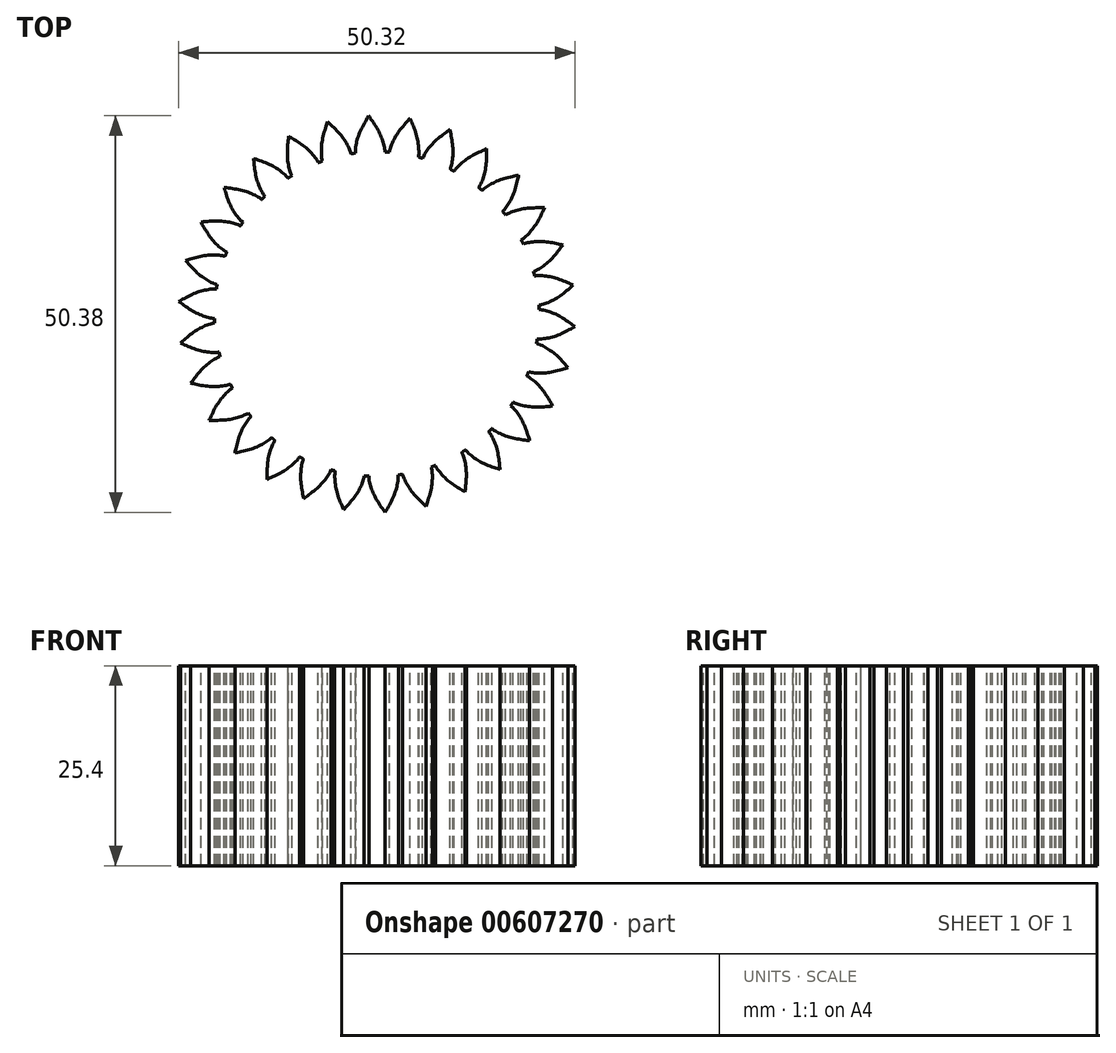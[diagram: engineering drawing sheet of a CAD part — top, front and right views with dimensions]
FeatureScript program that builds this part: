
annotation { "Feature Type Name" : "Feature", "Feature Type Description" : "" }
export const myFeature = defineFeature(function(context is Context, id is Id, definition is map)
    precondition{}
    {
        {
            assignVariable(context, id + "F0", {"name" : "nt", "anyValue" : 30});
        }
        {
            var Q0;
            Q0=qCreatedBy(makeId("Top.planeOp"),FACE);
            var sketch = newSketch(context, id + "F1", { "sketchPlane" : qUnion([Q0])});
            skPoint(sketch, "E0", {"position": v(1.08, 20.6) * mm});
            skPoint(sketch, "E1", {"position": v(1.06, 20.92) * mm});
            skPoint(sketch, "E2", {"position": v(0.84, 21.88) * mm});
            skPoint(sketch, "E3", {"position": v(0.2, 23.39) * mm});
            skPoint(sketch, "E4", {"position": v(-1.05, 25.3) * mm});
            skCircle(sketch, "E5", {"center": v(0, 0) * mm, "radius": 20.62 * mm});
            skCircle(sketch, "E6", {"center": v(0, 0) * mm, "radius": 23.81 * mm, "construction": true});
            skCircle(sketch, "E7", {"center": v(0, 0) * mm, "radius": 30.2 * mm});
            skCircle(sketch, "E8", {"center": v(0, 0) * mm, "radius": 25.33 * mm});
            skFitSpline(sketch, "E9", {"points": [v(1.08, 20.6) * mm, v(1.06, 20.92) * mm, v(0.84, 21.88) * mm, v(0.2, 23.39) * mm, v(-1.05, 25.3) * mm], "startDerivative": vector(-0.05, 2.19) * mm, "endDerivative": vector(-3.92, 5.61) * mm});
            skLineSegment(sketch, "E10", {"start": v(-1.05, 25.3) * mm, "end": v(-0.85, 20.6) * mm});
            skSolve(sketch);
        }
        {
            var Q0;
            {var subQ1=sQuery(id+"F1.wireOp",EDGE,"E9");Q0=makeQuery(id+"F1.imprint","IMPRINT",FACE,{"disambiguationData":[TD([[makeQuery(id+"F1.imprint","IMPRINT",EDGE,{"derivedFrom":subQ1}),1.0]])]});}
            extrude(context, id + "F2", {"entities" : qUnion([Q0]), "depth" : 25.4 * mm});
        }
        {
            var Q0;
            Q0=makeQuery(id+"F2.opExtrude","CAP_FACE",FACE,{"disambiguationData":[OSD([sQuery(id+"F1.wireOp",EDGE,"E5"),sQuery(id+"F1.wireOp",EDGE,"E9"),sQuery(id+"F1.wireOp",EDGE,"E10")])],"isStart":false});
            var sketch = newSketch(context, id + "F3", { "sketchPlane" : qUnion([Q0])});
            skFitSpline(sketch, "E11.0", {"points": [v(1.08, 20.6) * mm, v(1.08, 20.69) * mm, v(1.07, 20.95) * mm, v(0.85, 21.96) * mm, v(0.25, 23.46) * mm, v(-0.6, 24.66) * mm, v(-1.05, 25.3) * mm]});
            skFitSpline(sketch, "E12.0", {"points": [v(1.02, 20.6) * mm, v(1.01, 20.68) * mm, v(1.01, 20.86) * mm, v(0.92, 21.34) * mm, v(0.76, 21.93) * mm, v(0.54, 22.56) * mm, v(0.24, 23.2) * mm, v(-0.15, 23.88) * mm, v(-0.6, 24.57) * mm, v(-0.94, 25.04) * mm, v(-1.1, 25.27) * mm]});
            skLineSegment(sketch, "E13", {"start": v(-1.05, 25.3) * mm, "end": v(-1.1, 25.27) * mm});
            skLineSegment(sketch, "E14", {"start": v(1.08, 20.6) * mm, "end": v(1.02, 20.6) * mm});
            skSolve(sketch);
        }
        {
            var Q0;
            {var subQ3=sQuery(id+"F3.wireOp",EDGE,"E11.0");Q0=makeQuery(id+"F3.imprint","IMPRINT",FACE,{"disambiguationData":[TD([[makeQuery(id+"F3.imprint","IMPRINT",EDGE,{"derivedFrom":subQ3}),1.0]])]});}
            extrude(context, id + "F4", {"entities" : qUnion([Q0]), "operationType" : NewBodyOperationType.REMOVE, "endBound" : BoundingType.THROUGH_ALL, "oppositeDirection" : true, "depth" : 25.4 * mm});
        }
        {
            var Q0;
            Q0=makeQuery(id+"F2.opExtrude","SWEPT_BODY",BODY,{"disambiguationData":[OSD([sQuery(id+"F1.wireOp",EDGE,"E5"),sQuery(id+"F1.wireOp",EDGE,"E9"),sQuery(id+"F1.wireOp",EDGE,"E10")])]});
            var Q1;
            Q1=makeQuery(id+"F2.opExtrude","SWEPT_FACE",FACE,{"disambiguationData":[OSD([sQuery(id+"F1.wireOp",EDGE,"E10")])]});
            mirror(context, id + "F5", {"operationType" : NewBodyOperationType.ADD, "entities" : qUnion([Q0]), "mirrorPlane" : qUnion([Q1])});
        }
        {
            var Q0;
            {var subQ0=makeQuery(id+"F2.opExtrude","CAP_FACE",FACE,{"disambiguationData":[OSD([sQuery(id+"F1.wireOp",EDGE,"E5"),sQuery(id+"F1.wireOp",EDGE,"E9"),sQuery(id+"F1.wireOp",EDGE,"E10")])],"isStart":false});Q0=makeQuery(id+"F5.boolean.opBoolean","MERGE",FACE,{"derivedFrom":[subQ0,makeQuery(id+"F5.opPattern","COPY",FACE,{"derivedFrom":subQ0,"instanceName":"1"})]});}
            var sketch = newSketch(context, id + "F6", { "sketchPlane" : qUnion([Q0])});
            skCircle(sketch, "E15", {"center": v(0, 0) * mm, "radius": 20.62 * mm});
            skSolve(sketch);
        }
        {
            var Q0;
            Q0=qSketchRegion(id+"F6",true);
            var Q1;
            {var subQ0=makeQuery(id+"F2.opExtrude","CAP_FACE",FACE,{"disambiguationData":[OSD([sQuery(id+"F1.wireOp",EDGE,"E5"),sQuery(id+"F1.wireOp",EDGE,"E9"),sQuery(id+"F1.wireOp",EDGE,"E10")])],"isStart":true});Q1=makeQuery(id+"F5.boolean.opBoolean","MERGE",FACE,{"derivedFrom":[subQ0,makeQuery(id+"F5.opPattern","COPY",FACE,{"derivedFrom":subQ0,"instanceName":"1"})]});}
            extrude(context, id + "F7", {"entities" : qUnion([Q0]), "endBound" : BoundingType.UP_TO_SURFACE, "oppositeDirection" : true, "endBoundEntityFace" : qUnion([Q1]), "depth" : 25.4 * mm});
        }
        {
            var Q0;
            Q0=makeQuery(id+"F2.opExtrude","SWEPT_BODY",BODY,{"disambiguationData":[OSD([sQuery(id+"F1.wireOp",EDGE,"E5"),sQuery(id+"F1.wireOp",EDGE,"E9"),sQuery(id+"F1.wireOp",EDGE,"E10")])]});
            var Q1;
            {var subQ0=makeQuery(id+"F2.opExtrude","SWEPT_FACE",FACE,{"disambiguationData":[OSD([sQuery(id+"F1.wireOp",EDGE,"E5")])]});Q1=makeQuery(id+"F5.boolean.opBoolean","MERGE",FACE,{"derivedFrom":[subQ0,makeQuery(id+"F5.opPattern","COPY",FACE,{"derivedFrom":subQ0,"instanceName":"1"})]});}
            circularPattern(context, id + "F8", {"operationType" : NewBodyOperationType.ADD, "entities" : qUnion([Q0]), "axis" : qUnion([Q1]), "angle" : 360 * degree, "instanceCount" : getVariable(context, 'nt'), "equalSpace" : true});
        }
    });
